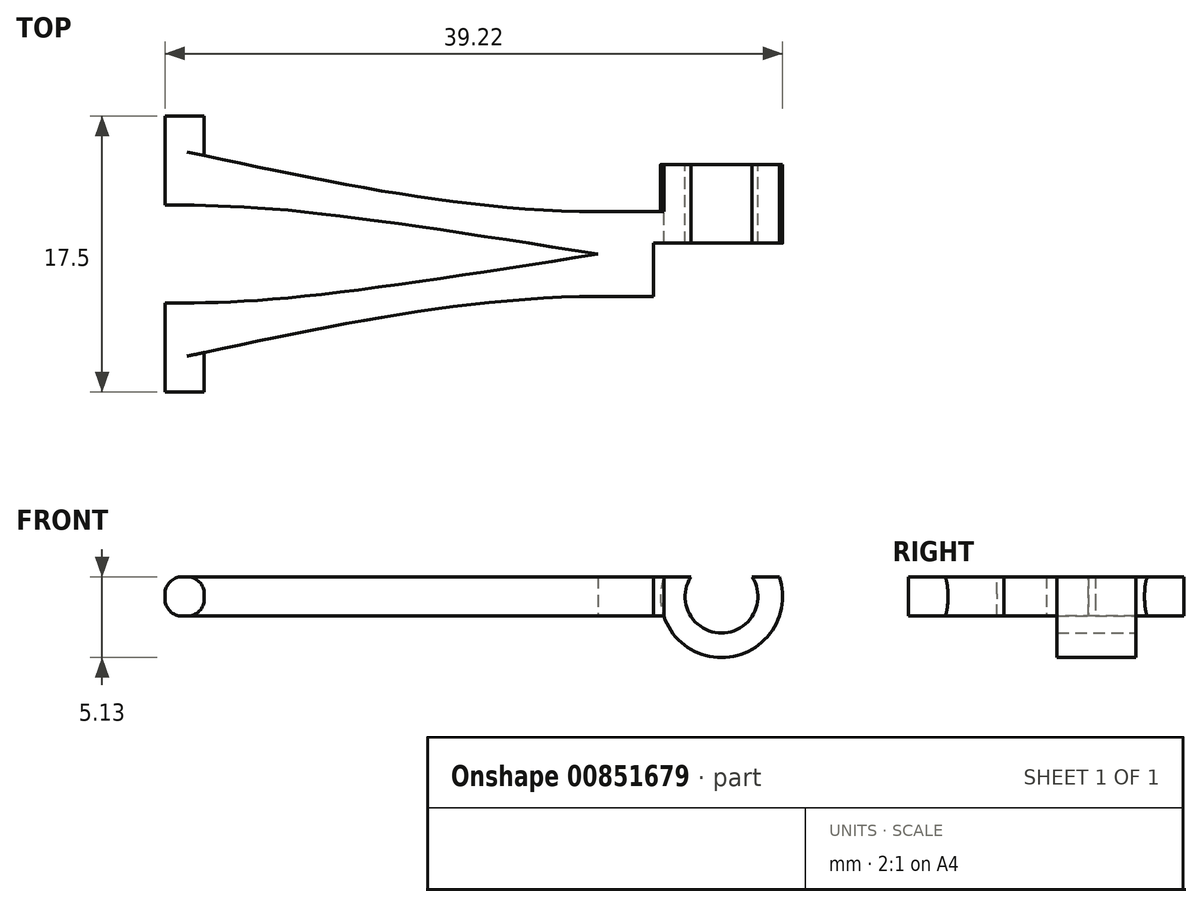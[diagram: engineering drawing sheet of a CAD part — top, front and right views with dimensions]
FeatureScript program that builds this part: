
annotation { "Feature Type Name" : "Feature", "Feature Type Description" : "" }
export const myFeature = defineFeature(function(context is Context, id is Id, definition is map)
    precondition{}
    {
        {
            var Q0;
            Q0=qCreatedBy(makeId("Top.planeOp"),FACE);
            var sketch = newSketch(context, id + "F0", { "sketchPlane" : qUnion([Q0])});
            skLineSegment(sketch, "E0.right", {"start": v(-27.5, -6.25) * mm, "end": v(-27.5, -3.12) * mm});
            skPoint(sketch, "E0.middle", {"position": v(0, 0) * mm});
            skLineSegment(sketch, "E1.top", {"start": v(-27.5, 8.75) * mm, "end": v(-25, 8.75) * mm});
            skLineSegment(sketch, "E1.left", {"start": v(-27.5, 6.25) * mm, "end": v(-27.5, 8.75) * mm});
            skLineSegment(sketch, "E1.right", {"start": v(-25, 6.25) * mm, "end": v(-25, 8.75) * mm});
            skFitSpline(sketch, "E2", {"points": [v(-25, 6.25) * mm, v(0, 2.69) * mm, v(27.5, 6.25) * mm], "startDerivative": vector(50.58, -10.78) * mm, "endDerivative": vector(54.4, 10.61) * mm});
            skLineSegment(sketch, "E3.MirrorCS", {"start": v(-25, -6.25) * mm, "end": v(-25, -8.75) * mm});
            skLineSegment(sketch, "E4.MirrorCS", {"start": v(-27.5, -8.75) * mm, "end": v(-25, -8.75) * mm});
            skLineSegment(sketch, "E5.MirrorCS", {"start": v(-27.5, -6.25) * mm, "end": v(-27.5, -8.75) * mm});
            skFitSpline(sketch, "E6.MirrorCS", {"points": [v(-25, -6.25) * mm, v(0, -2.69) * mm, v(27.5, -6.25) * mm], "startDerivative": vector(50.58, 10.78) * mm, "endDerivative": vector(54.4, -10.61) * mm});
            skFitSpline(sketch, "E7", {"points": [v(-27.5, 3.12) * mm, v(-19.83, 2.8) * mm, v(0, 0) * mm], "startDerivative": vector(17.76, -0.15) * mm, "endDerivative": vector(35.83, -5.66) * mm});
            skFitSpline(sketch, "E8.MirrorCS", {"points": [v(-27.5, -3.12) * mm, v(-19.83, -2.8) * mm, v(0, 0) * mm], "startDerivative": vector(17.76, 0.15) * mm, "endDerivative": vector(35.83, 5.66) * mm});
            skLineSegment(sketch, "E9.trimOffspring", {"start": v(-27.5, 3.12) * mm, "end": v(-27.5, 6.25) * mm});
            skLineSegment(sketch, "E10", {"start": v(0, 2.69) * mm, "end": v(7.14, 2.69) * mm});
            skLineSegment(sketch, "E11.MirrorCS", {"start": v(0, -2.69) * mm, "end": v(7.14, -2.69) * mm});
            skLineSegment(sketch, "E12", {"start": v(7.14, -2.69) * mm, "end": v(7.14, 2.69) * mm});
            skPoint(sketch, "E0.left.end.orphan", {"position": v(27.5, 2.69) * mm});
            skPoint(sketch, "E0.left.start.orphan", {"position": v(27.5, -2.69) * mm});
            skSolve(sketch);
        }
        {
            var Q0;
            {var subQ6=sQuery(id+"F0.wireOp",EDGE,"E0.left");Q0=makeQuery(id+"F0.imprint","IMPRINT",FACE,{"disambiguationData":[TD([[makeQuery(id+"F0.imprint","IMPRINT",EDGE,{"derivedFrom":subQ6}),1.0]])]});}
            var Q1;
            Q1=makeQuery(id+"F0.imprint","IMPRINT",FACE,{"disambiguationData":[TD([[makeQuery(id+"F0.imprint","IMPRINT",EDGE,{"derivedFrom":sQuery(id+"F0.wireOp",EDGE,"E0.right")}),-1.0]])]});
            extrude(context, id + "F1", {"entities" : qUnion([Q0, Q1]), "depth" : 2.5 * mm, "offsetDistance" : 25 * mm});
        }
        {
            var Q0;
            Q0=makeQuery(id+"F1.opExtrude","CAP_EDGE",EDGE,{"disambiguationData":[OSD([sQuery(id+"F0.wireOp",EDGE,"E0.right"),sQuery(id+"F0.wireOp",EDGE,"E5.MirrorCS")])],"isStart":false});
            var Q1;
            Q1=makeQuery(id+"F1.opExtrude","CAP_EDGE",EDGE,{"disambiguationData":[OSD([sQuery(id+"F0.wireOp",EDGE,"E0.right"),sQuery(id+"F0.wireOp",EDGE,"E5.MirrorCS")])],"isStart":true});
            var Q2;
            Q2=makeQuery(id+"F1.opExtrude","CAP_EDGE",EDGE,{"disambiguationData":[OSD([sQuery(id+"F0.wireOp",EDGE,"E1.left"),sQuery(id+"F0.wireOp",EDGE,"E9.trimOffspring")])],"isStart":true});
            var Q3;
            Q3=makeQuery(id+"F1.opExtrude","CAP_EDGE",EDGE,{"disambiguationData":[OSD([sQuery(id+"F0.wireOp",EDGE,"E1.left"),sQuery(id+"F0.wireOp",EDGE,"E9.trimOffspring")])],"isStart":false});
            var Q4;
            Q4=makeQuery(id+"F1.opExtrude","CAP_EDGE",EDGE,{"disambiguationData":[OSD([sQuery(id+"F0.wireOp",EDGE,"E1.right")])],"isStart":false});
            var Q5;
            Q5=makeQuery(id+"F1.opExtrude","CAP_EDGE",EDGE,{"disambiguationData":[OSD([sQuery(id+"F0.wireOp",EDGE,"E3.MirrorCS")])],"isStart":true});
            var Q6;
            Q6=makeQuery(id+"F1.opExtrude","CAP_EDGE",EDGE,{"disambiguationData":[OSD([sQuery(id+"F0.wireOp",EDGE,"E1.right")])],"isStart":true});
            var Q7;
            Q7=makeQuery(id+"F1.opExtrude","CAP_EDGE",EDGE,{"disambiguationData":[OSD([sQuery(id+"F0.wireOp",EDGE,"E3.MirrorCS")])],"isStart":false});
            fillet(context, id + "F2", {"entities" : qUnion([Q0, Q1, Q2, Q3, Q4, Q5, Q6, Q7]), "radius" : 1.1 * mm, "tangentPropagation" : true, "allowEdgeOverflow" : false});
        }
        {
            var Q0;
            Q0=makeQuery(id+"F1.opExtrude","SWEPT_FACE",FACE,{"disambiguationData":[OSD([sQuery(id+"F0.wireOp",EDGE,"E10")])]});
            var sketch = newSketch(context, id + "F3", { "sketchPlane" : qUnion([Q0])});
            skArc(sketch, "E13", {"start": v(-9.8, 2.5) * mm, "mid": v(-7.85, -1.07) * mm, "end": v(-5.9, 2.5) * mm});
            skArc(sketch, "E14", {"start": v(-11.52, 2.5) * mm, "mid": v(-7.85, -2.63) * mm, "end": v(-4.18, 2.5) * mm});
            skPoint(sketch, "E15.orphan", {"position": v(-7.85, 0) * mm});
            skPoint(sketch, "E16.end.orphan", {"position": v(-7.85, 2.5) * mm});
            skLineSegment(sketch, "E17", {"start": v(-4.18, 2.5) * mm, "end": v(-11.52, 2.5) * mm});
            skSolve(sketch);
        }
        {
            var Q0;
            {var subQ2=sQuery(id+"F0.wireOp",EDGE,"E10");var subQ6=makeQuery(id+"F1.opExtrude","SWEPT_EDGE",EDGE,{"disambiguationData":[OSD([sQuery(id+"F0.wireOp",EDGE,"E0.left"),subQ2])]});Q0=makeQuery(id+"F3.imprint","IMPRINT",FACE,{"disambiguationData":[TD([[makeQuery(id+"F3.imprint","IMPRINT",EDGE,{"derivedFrom":subQ6}),1.0]])]});}
            extrude(context, id + "F4", {"entities" : qUnion([Q0]), "operationType" : NewBodyOperationType.REMOVE, "oppositeDirection" : true, "depth" : 5.4 * mm, "offsetDistance" : 25 * mm});
        }
        {
            var Q0;
            {var subQ0=sQuery(id+"F3.wireOp",EDGE,"3vo2jaRf-ucX2-ZlKN-bR0O-p1SpFn3305d9");Q0=makeQuery(id+"F3.imprint","IMPRINT",FACE,{"disambiguationData":[TD([[makeQuery(id+"F3.imprint","IMPRINT",EDGE,{"derivedFrom":subQ0}),1.0]])]});}
            var Q1;
            {var subQ0=sQuery(id+"F3.wireOp",EDGE,"E17");var subQ1=sQuery(id+"F3.wireOp",EDGE,"E13");var subQ2=makeQuery(id+"F3.imprint","INTERSECT",VERTEX,{"disambiguationData":[OD(0.0)],"derivedFrom":[subQ1,subQ0]});Q1=makeQuery(id+"F3.imprint","IMPRINT",FACE,{"disambiguationData":[TD([[makeQuery(id+"F3.imprint","IMPRINT",EDGE,{"disambiguationData":[TD([[subQ2,-1.0]])],"derivedFrom":subQ1}),1.0]])]});}
            extrude(context, id + "F5", {"entities" : qUnion([Q0, Q1]), "operationType" : NewBodyOperationType.REMOVE, "depth" : -5.4 * mm, "offsetDistance" : 25 * mm});
        }
        {
            var Q0;
            {var subQ0=sQuery(id+"F3.wireOp",EDGE,"E17");var subQ1=sQuery(id+"F3.wireOp",EDGE,"E13");var subQ2=makeQuery(id+"F3.imprint","INTERSECT",VERTEX,{"disambiguationData":[OD(0.0)],"derivedFrom":[subQ1,subQ0]});Q0=makeQuery(id+"F3.imprint","IMPRINT",FACE,{"disambiguationData":[TD([[makeQuery(id+"F3.imprint","IMPRINT",EDGE,{"disambiguationData":[TD([[subQ2,-1.0]])],"derivedFrom":subQ1}),-1.0]])]});}
            var Q1;
            {var subQ0=sQuery(id+"F3.wireOp",EDGE,"E17");var subQ1=sQuery(id+"F3.wireOp",EDGE,"E13");var subQ2=makeQuery(id+"F3.imprint","INTERSECT",VERTEX,{"disambiguationData":[OD(1.0)],"derivedFrom":[subQ1,subQ0]});Q1=makeQuery(id+"F3.imprint","IMPRINT",FACE,{"disambiguationData":[TD([[makeQuery(id+"F3.imprint","IMPRINT",EDGE,{"disambiguationData":[TD([[subQ2,1.0]])],"derivedFrom":subQ1}),-1.0]])]});}
            extrude(context, id + "F6", {"entities" : qUnion([Q0, Q1]), "operationType" : NewBodyOperationType.ADD, "depth" : 3 * mm, "offsetDistance" : 25 * mm});
        }
        {
            var Q0;
            {var subQ0=sQuery(id+"F3.wireOp",EDGE,"E17");var subQ1=sQuery(id+"F3.wireOp",EDGE,"E13");var subQ2=makeQuery(id+"F3.imprint","INTERSECT",VERTEX,{"disambiguationData":[OD(0.0)],"derivedFrom":[subQ1,subQ0]});Q0=makeQuery(id+"F3.imprint","IMPRINT",FACE,{"disambiguationData":[TD([[makeQuery(id+"F3.imprint","IMPRINT",EDGE,{"disambiguationData":[TD([[subQ2,-1.0]])],"derivedFrom":subQ1}),-1.0]])]});}
            extrude(context, id + "F7", {"entities" : qUnion([Q0]), "operationType" : NewBodyOperationType.ADD, "depth" : -2 * mm, "offsetDistance" : 25 * mm});
        }
        {
            var Q0;
            Q0=makeQuery(id+"F1.opExtrude","CAP_FACE",FACE,{"disambiguationData":[OSD([sQuery(id+"F0.wireOp",EDGE,"E0.right"),sQuery(id+"F0.wireOp",EDGE,"E1.top"),sQuery(id+"F0.wireOp",EDGE,"E1.left"),sQuery(id+"F0.wireOp",EDGE,"E1.right"),sQuery(id+"F0.wireOp",EDGE,"E2"),sQuery(id+"F0.wireOp",EDGE,"E3.MirrorCS"),sQuery(id+"F0.wireOp",EDGE,"E4.MirrorCS"),sQuery(id+"F0.wireOp",EDGE,"E5.MirrorCS"),sQuery(id+"F0.wireOp",EDGE,"E6.MirrorCS"),sQuery(id+"F0.wireOp",EDGE,"E7"),sQuery(id+"F0.wireOp",EDGE,"E8.MirrorCS"),sQuery(id+"F0.wireOp",EDGE,"E9.trimOffspring"),sQuery(id+"F0.wireOp",EDGE,"E10"),sQuery(id+"F0.wireOp",EDGE,"E11.MirrorCS"),sQuery(id+"F0.wireOp",EDGE,"E12")])],"isStart":true});
            var sketch = newSketch(context, id + "F8", { "sketchPlane" : qUnion([Q0])});
            skLineSegment(sketch, "E18.bottom", {"start": v(5.9, 2.69) * mm, "end": v(3.54, 2.69) * mm});
            skLineSegment(sketch, "E18.top", {"start": v(5.9, -0.7) * mm, "end": v(3.54, -0.7) * mm});
            skLineSegment(sketch, "E18.left", {"start": v(5.9, 2.69) * mm, "end": v(5.9, -0.7) * mm});
            skLineSegment(sketch, "E18.right", {"start": v(3.54, 2.69) * mm, "end": v(3.54, -0.7) * mm});
            skSolve(sketch);
        }
        {
            var Q0;
            {var subQ1=sQuery(id+"F8.wireOp",EDGE,"E18.bottom");Q0=makeQuery(id+"F8.imprint","IMPRINT",FACE,{"disambiguationData":[TD([[makeQuery(id+"F8.imprint","IMPRINT",EDGE,{"derivedFrom":subQ1}),-1.0]])]});}
            extrude(context, id + "F9", {"entities" : qUnion([Q0]), "operationType" : NewBodyOperationType.REMOVE, "oppositeDirection" : true, "depth" : 3 * mm, "offsetDistance" : 25 * mm});
        }
    });
